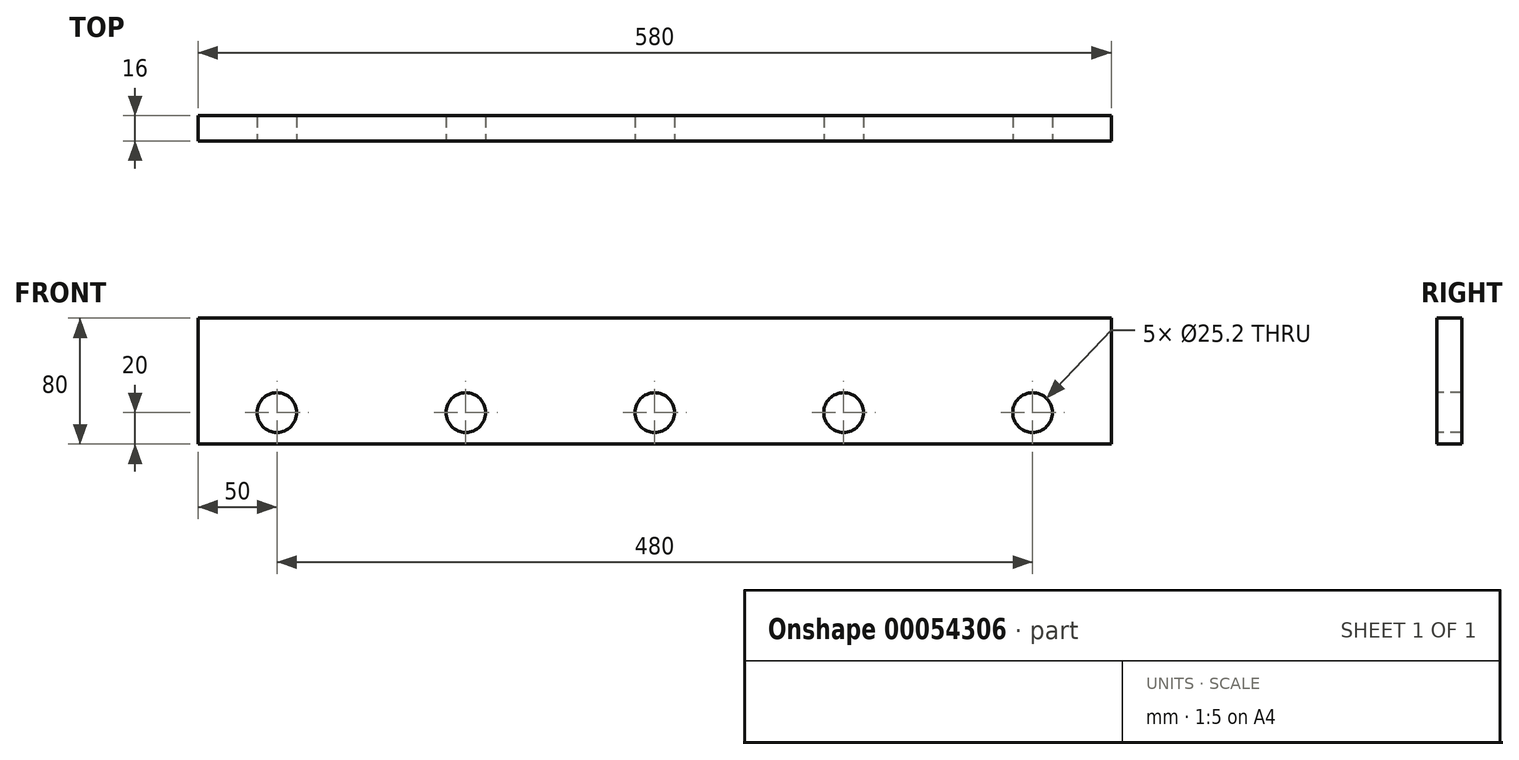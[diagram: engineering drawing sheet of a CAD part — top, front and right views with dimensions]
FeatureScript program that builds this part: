
annotation { "Feature Type Name" : "Feature", "Feature Type Description" : "" }
export const myFeature = defineFeature(function(context is Context, id is Id, definition is map)
    precondition{}
    {
        {
            var Q0;
            Q0=qCreatedBy(makeId("Front.planeOp"),FACE);
            var sketch = newSketch(context, id + "F0", { "sketchPlane" : qUnion([Q0])});
            skLineSegment(sketch, "E0.rect.bottom", {"start": v(-290, 40) * mm, "end": v(290, 40) * mm});
            skLineSegment(sketch, "E0.rect.top", {"start": v(-290, -40) * mm, "end": v(290, -40) * mm});
            skLineSegment(sketch, "E0.rect.left", {"start": v(-290, 40) * mm, "end": v(-290, -40) * mm});
            skLineSegment(sketch, "E0.rect.right", {"start": v(290, 40) * mm, "end": v(290, -40) * mm});
            skPoint(sketch, "E0.rect.middle", {"position": v(0, 0) * mm});
            skCircle(sketch, "E1", {"center": v(-240, -20) * mm, "radius": 12.6 * mm});
            skCircle(sketch, "E2", {"center": v(-120, -20) * mm, "radius": 12.6 * mm});
            skCircle(sketch, "E3", {"center": v(0, -20) * mm, "radius": 12.6 * mm});
            skCircle(sketch, "E4", {"center": v(120, -20) * mm, "radius": 12.6 * mm});
            skCircle(sketch, "E5", {"center": v(240, -20) * mm, "radius": 12.6 * mm});
            skSolve(sketch);
        }
        {
            var Q0;
            Q0=makeQuery(id+"F0.imprint","IMPRINT",FACE,{"disambiguationData":[TD([[makeQuery(id+"F0.imprint","IMPRINT",EDGE,{"derivedFrom":sQuery(id+"F0.wireOp",EDGE,"E0.rect.bottom")}),-1.0]])]});
            extrude(context, id + "F1", {"entities" : qUnion([Q0]), "oppositeDirection" : true, "depth" : 16 * mm});
        }
    });
